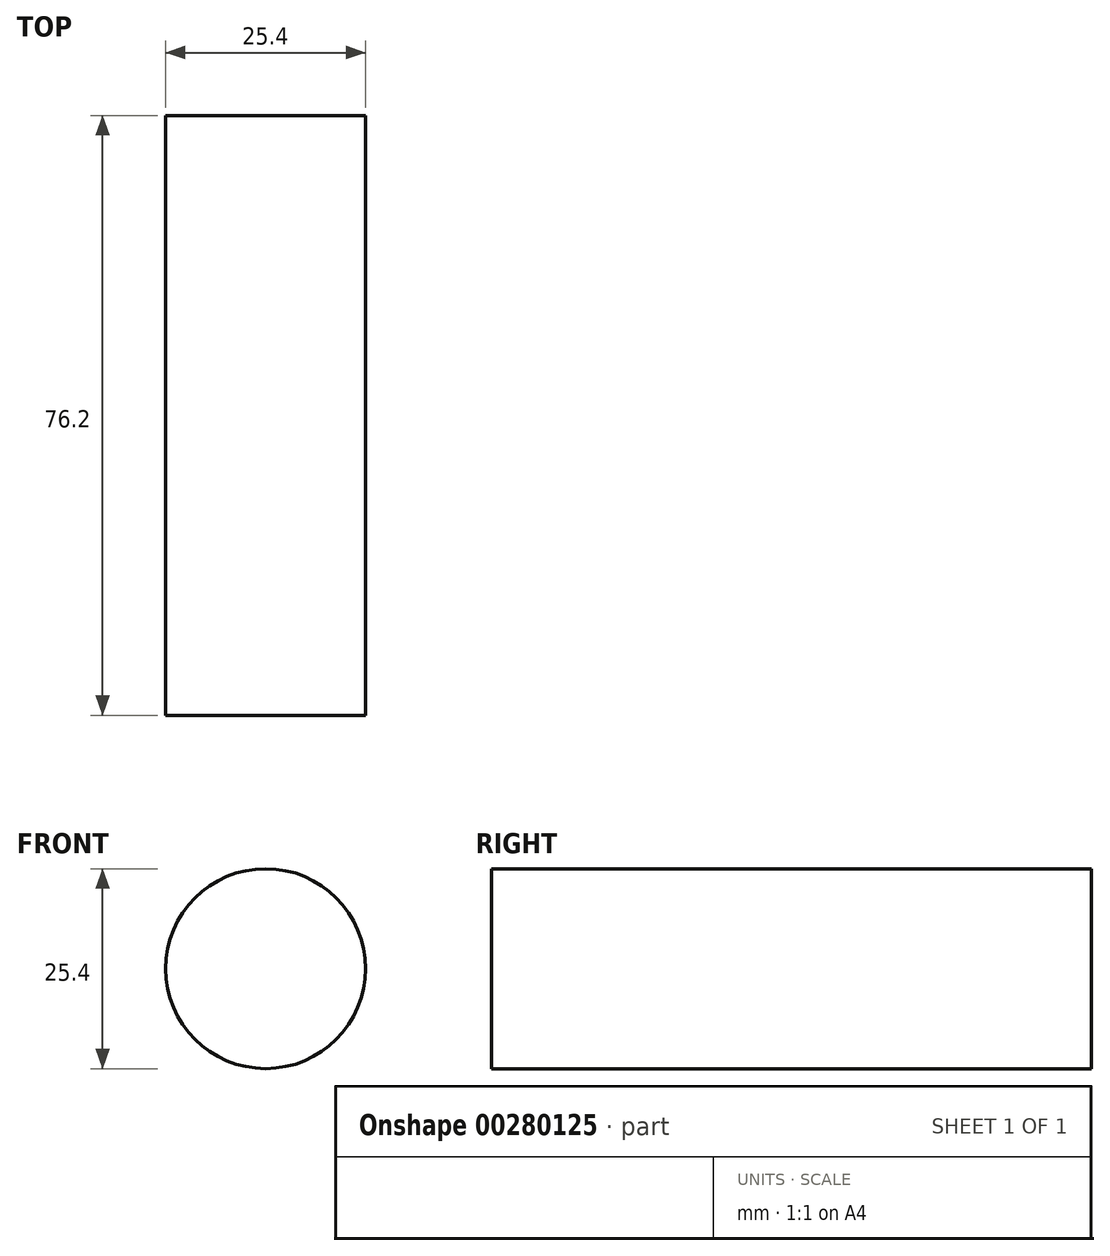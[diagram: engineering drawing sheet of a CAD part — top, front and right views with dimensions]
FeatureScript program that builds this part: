
annotation { "Feature Type Name" : "Feature", "Feature Type Description" : "" }
export const myFeature = defineFeature(function(context is Context, id is Id, definition is map)
    precondition{}
    {
        {
            var Q0;
            Q0=qCreatedBy(makeId("Front.planeOp"),FACE);
            var sketch = newSketch(context, id + "F0", { "sketchPlane" : qUnion([Q0])});
            skCircle(sketch, "E0", {"center": v(-37.88, 37.66) * mm, "radius": 12.7 * mm});
            skSolve(sketch);
        }
        {
            var Q0;
            Q0 = qSketchRegion(id + "F0", true);
            extrude(context, id + "F1", {"entities" : qUnion([Q0]), "depth" : 76.2 * mm});
        }
    });
